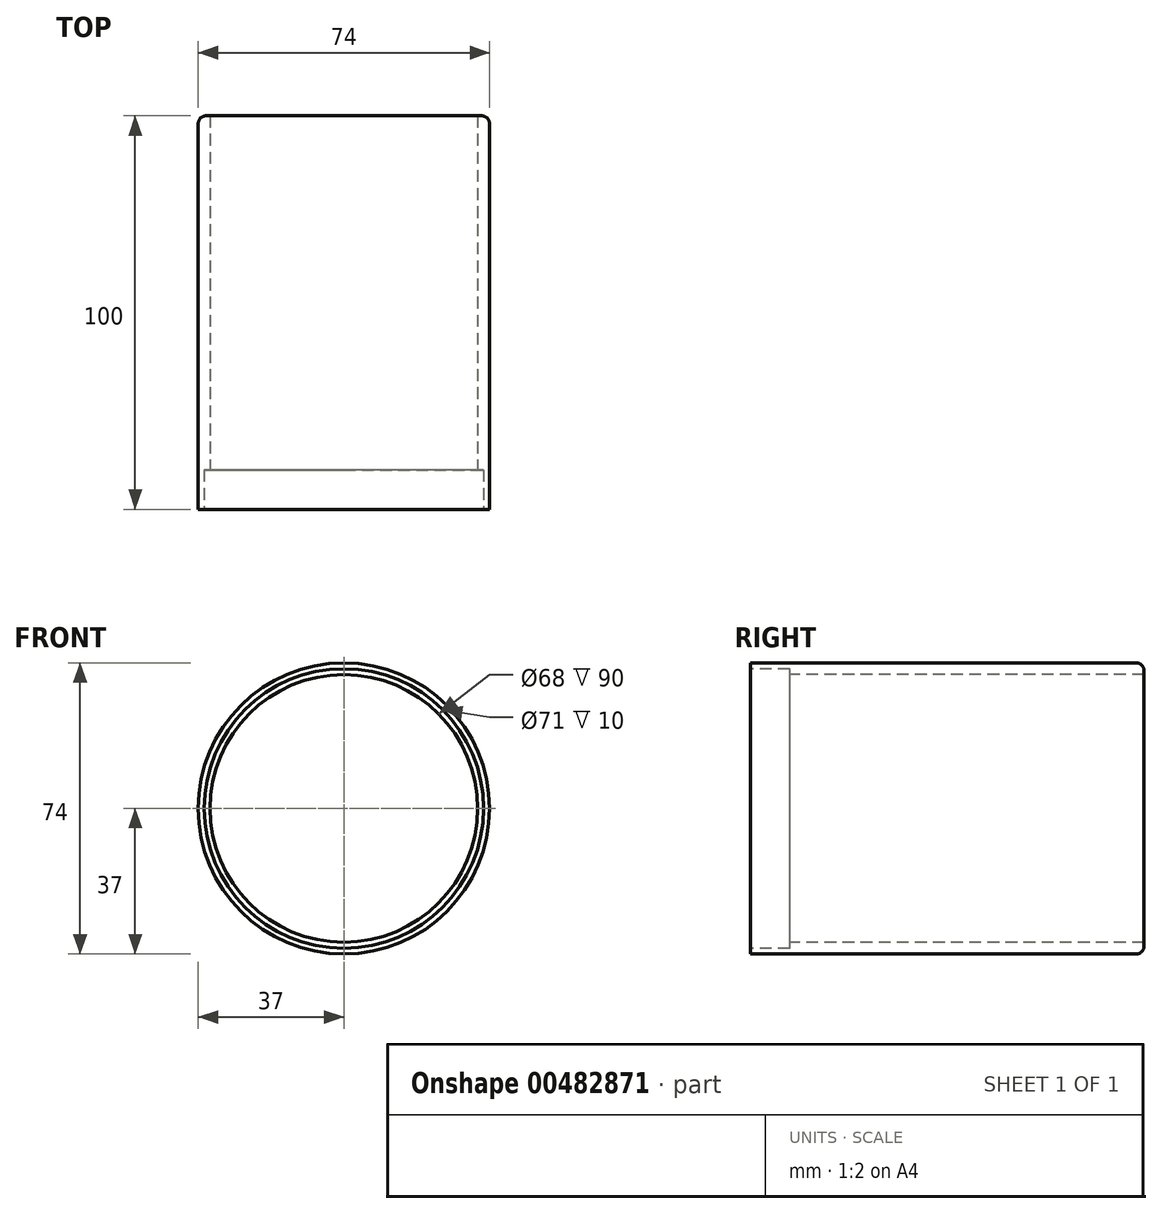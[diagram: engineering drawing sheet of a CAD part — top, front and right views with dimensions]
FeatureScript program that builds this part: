
annotation { "Feature Type Name" : "Feature", "Feature Type Description" : "" }
export const myFeature = defineFeature(function(context is Context, id is Id, definition is map)
    precondition{}
    {
        {
            var Q0;
            Q0=qCreatedBy(makeId("Front.planeOp"),FACE);
            var sketch = newSketch(context, id + "F0", { "sketchPlane" : qUnion([Q0])});
            skCircle(sketch, "E0", {"center": v(0, 0) * mm, "radius": 37 * mm});
            skSolve(sketch);
        }
        {
            var Q0;
            Q0=makeQuery(id+"F0.imprint","IMPRINT",FACE,{"disambiguationData":[TD([[makeQuery(id+"F0.imprint","IMPRINT",EDGE,{"derivedFrom":sQuery(id+"F0.wireOp",EDGE,"E0")}),1.0]])]});
            extrude(context, id + "F1", {"entities" : qUnion([Q0]), "oppositeDirection" : true, "depth" : 100 * mm});
        }
        {
            var Q0;
            Q0=makeQuery(id+"F1.opExtrude","CAP_FACE",FACE,{"disambiguationData":[OSD([sQuery(id+"F0.wireOp",EDGE,"E0")])],"isStart":true});
            var sketch = newSketch(context, id + "F2", { "sketchPlane" : qUnion([Q0])});
            skCircle(sketch, "E1", {"center": v(0, 0) * mm, "radius": 34 * mm});
            skSolve(sketch);
        }
        {
            var Q0;
            Q0 = qSketchRegion(id + "F2", true);
            extrude(context, id + "F3", {"entities" : qUnion([Q0]), "operationType" : NewBodyOperationType.REMOVE, "oppositeDirection" : true, "depth" : 245 * mm});
        }
        {
            var Q0;
            Q0=makeQuery(id+"F1.opExtrude","CAP_EDGE",EDGE,{"disambiguationData":[OSD([sQuery(id+"F0.wireOp",EDGE,"E0")])],"isStart":false});
            fillet(context, id + "F4", {"entities" : qUnion([Q0]), "radius" : 2 * mm, "tangentPropagation" : true, "allowEdgeOverflow" : false});
        }
        {
            var Q0;
            Q0=qCreatedBy(makeId("Front.planeOp"),FACE);
            var sketch = newSketch(context, id + "F5", { "sketchPlane" : qUnion([Q0])});
            skCircle(sketch, "E2", {"center": v(0, 0) * mm, "radius": 35.5 * mm});
            skSolve(sketch);
        }
        {
            var Q0;
            Q0=makeQuery(id+"F5.imprint","IMPRINT",FACE,{"disambiguationData":[TD([[makeQuery(id+"F5.imprint","IMPRINT",EDGE,{"derivedFrom":sQuery(id+"F5.wireOp",EDGE,"E2")}),1.0]])]});
            extrude(context, id + "F6", {"entities" : qUnion([Q0]), "operationType" : NewBodyOperationType.REMOVE, "oppositeDirection" : true, "depth" : 10 * mm});
        }
    });
